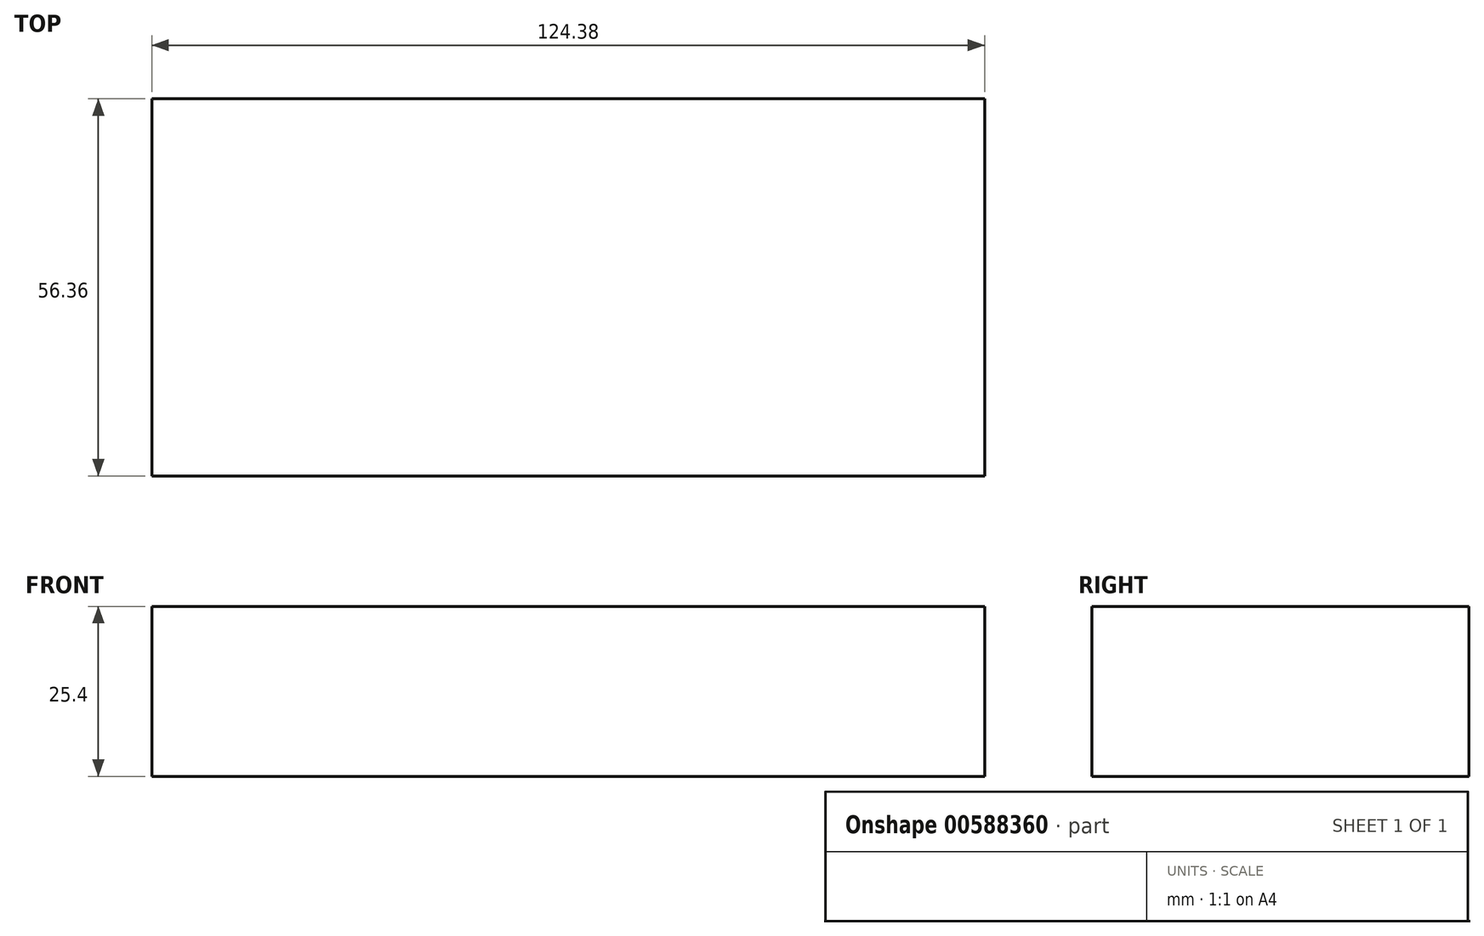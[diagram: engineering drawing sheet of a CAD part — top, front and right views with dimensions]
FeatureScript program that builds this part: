
annotation { "Feature Type Name" : "Feature", "Feature Type Description" : "" }
export const myFeature = defineFeature(function(context is Context, id is Id, definition is map)
    precondition{}
    {
        {
            var Q0;
            Q0=qCreatedBy(makeId("Top.planeOp"),FACE);
            var sketch = newSketch(context, id + "F0", { "sketchPlane" : qUnion([Q0])});
            skLineSegment(sketch, "E0.bottom", {"start": v(-54.82, 30.53) * mm, "end": v(69.56, 30.53) * mm});
            skLineSegment(sketch, "E0.top", {"start": v(-54.82, -25.83) * mm, "end": v(69.56, -25.83) * mm});
            skLineSegment(sketch, "E0.left", {"start": v(-54.82, 30.53) * mm, "end": v(-54.82, -25.83) * mm});
            skLineSegment(sketch, "E0.right", {"start": v(69.56, 30.53) * mm, "end": v(69.56, -25.83) * mm});
            skSolve(sketch);
        }
        {
            var Q0;
            Q0=makeQuery(id+"F0.imprint","IMPRINT",FACE,{"disambiguationData":[TD([[makeQuery(id+"F0.imprint","IMPRINT",EDGE,{"derivedFrom":sQuery(id+"F0.wireOp",EDGE,"E0.bottom")}),-1.0]])]});
            extrude(context, id + "F1", {"entities" : qUnion([Q0]), "depth" : 25.4 * mm, "offsetDistance" : 25.4 * mm});
        }
    });
